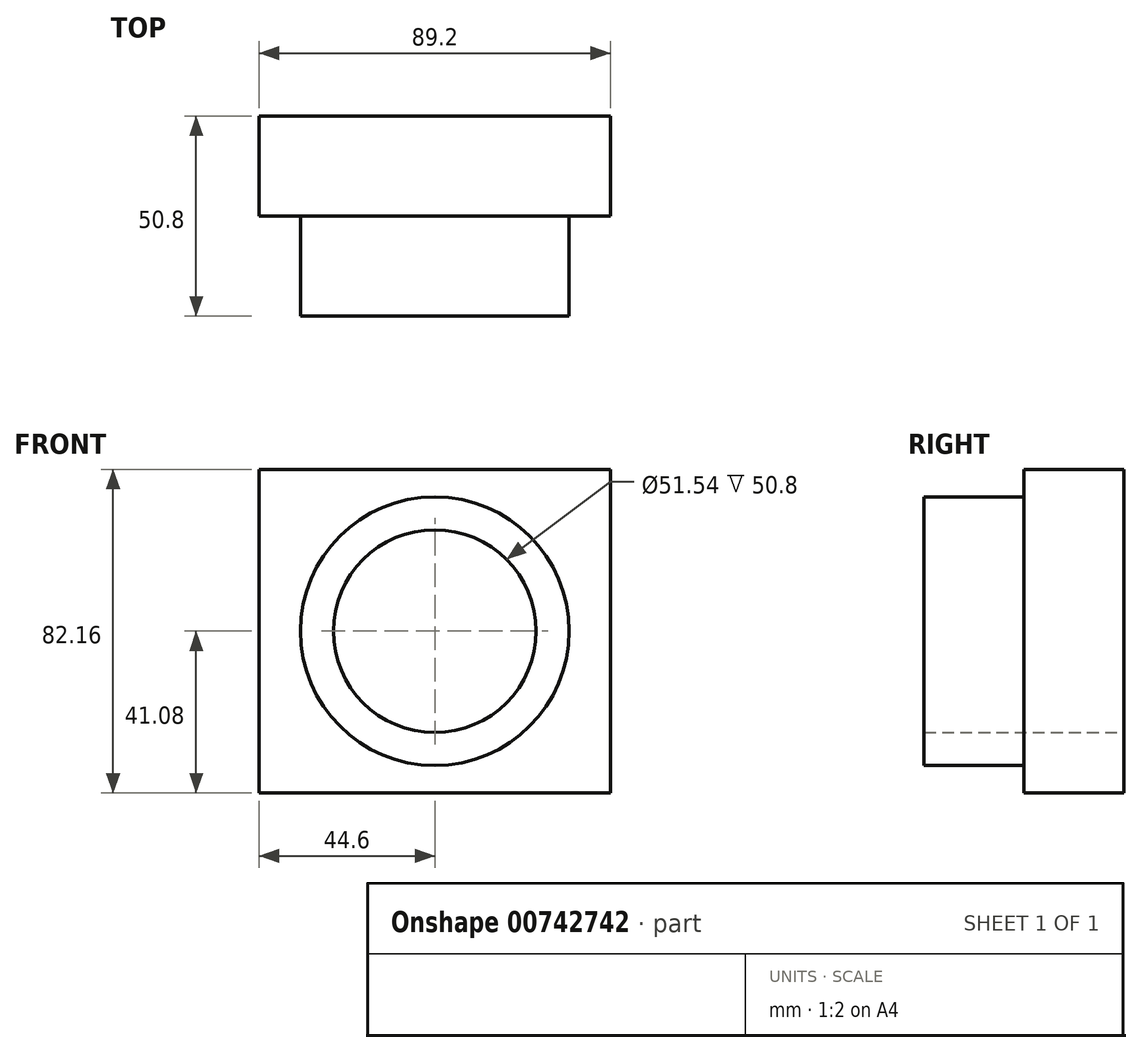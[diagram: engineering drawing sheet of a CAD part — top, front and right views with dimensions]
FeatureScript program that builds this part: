
annotation { "Feature Type Name" : "Feature", "Feature Type Description" : "" }
export const myFeature = defineFeature(function(context is Context, id is Id, definition is map)
    precondition{}
    {
        {
            var Q0;
            Q0=qCreatedBy(makeId("Front.planeOp"),FACE);
            var sketch = newSketch(context, id + "F0", { "sketchPlane" : qUnion([Q0])});
            skLineSegment(sketch, "E0.bottom", {"start": v(44.6, 41.08) * mm, "end": v(-44.6, 41.08) * mm});
            skLineSegment(sketch, "E0.top", {"start": v(44.6, -41.08) * mm, "end": v(-44.6, -41.08) * mm});
            skLineSegment(sketch, "E0.left", {"start": v(44.6, 41.08) * mm, "end": v(44.6, -41.08) * mm});
            skLineSegment(sketch, "E0.right", {"start": v(-44.6, 41.08) * mm, "end": v(-44.6, -41.08) * mm});
            skPoint(sketch, "E0.middle", {"position": v(0, 0) * mm});
            skSolve(sketch);
        }
        {
            var Q0;
            Q0=qCreatedBy(makeId("Front.planeOp"),FACE);
            var sketch = newSketch(context, id + "F1", { "sketchPlane" : qUnion([Q0])});
            skCircle(sketch, "E1", {"center": v(0, 0) * mm, "radius": 34.12 * mm});
            skCircle(sketch, "E2", {"center": v(0, 0) * mm, "radius": 25.77 * mm});
            skSolve(sketch);
        }
        {
            var Q0;
            Q0=makeQuery(id+"F1.imprint","IMPRINT",FACE,{"disambiguationData":[TD([[makeQuery(id+"F1.imprint","IMPRINT",EDGE,{"derivedFrom":sQuery(id+"F1.wireOp",EDGE,"E1")}),1.0]])]});
            extrude(context, id + "F2", {"entities" : qUnion([Q0]), "depth" : 50.8 * mm, "offsetDistance" : 25.4 * mm});
        }
        {
            var Q0;
            Q0=makeQuery(id+"F0.imprint","IMPRINT",FACE,{"disambiguationData":[TD([[makeQuery(id+"F0.imprint","IMPRINT",EDGE,{"derivedFrom":sQuery(id+"F0.wireOp",EDGE,"E0.bottom")}),1.0]])]});
            extrude(context, id + "F3", {"entities" : qUnion([Q0]), "operationType" : NewBodyOperationType.ADD, "depth" : 25.4 * mm, "offsetDistance" : 25.4 * mm});
        }
        {
            var Q0;
            Q0=makeQuery(id+"F3.boolean.opBoolean","SPLIT",FACE,{"disambiguationData":[TD([makeQuery(id+"F2.opExtrude","SWEPT_FACE",FACE,{"disambiguationData":[OSD([sQuery(id+"F1.wireOp",EDGE,"E2")])]})])],"derivedFrom":makeQuery(id+"F3.opExtrude","CAP_FACE",FACE,{"disambiguationData":[OSD([sQuery(id+"F0.wireOp",EDGE,"E0.bottom"),sQuery(id+"F0.wireOp",EDGE,"E0.top"),sQuery(id+"F0.wireOp",EDGE,"E0.left"),sQuery(id+"F0.wireOp",EDGE,"E0.right")])],"isStart":false})});
            extrude(context, id + "F4", {"entities" : qUnion([Q0]), "operationType" : NewBodyOperationType.REMOVE, "oppositeDirection" : true, "depth" : 25.4 * mm, "offsetDistance" : 25.4 * mm});
        }
    });
